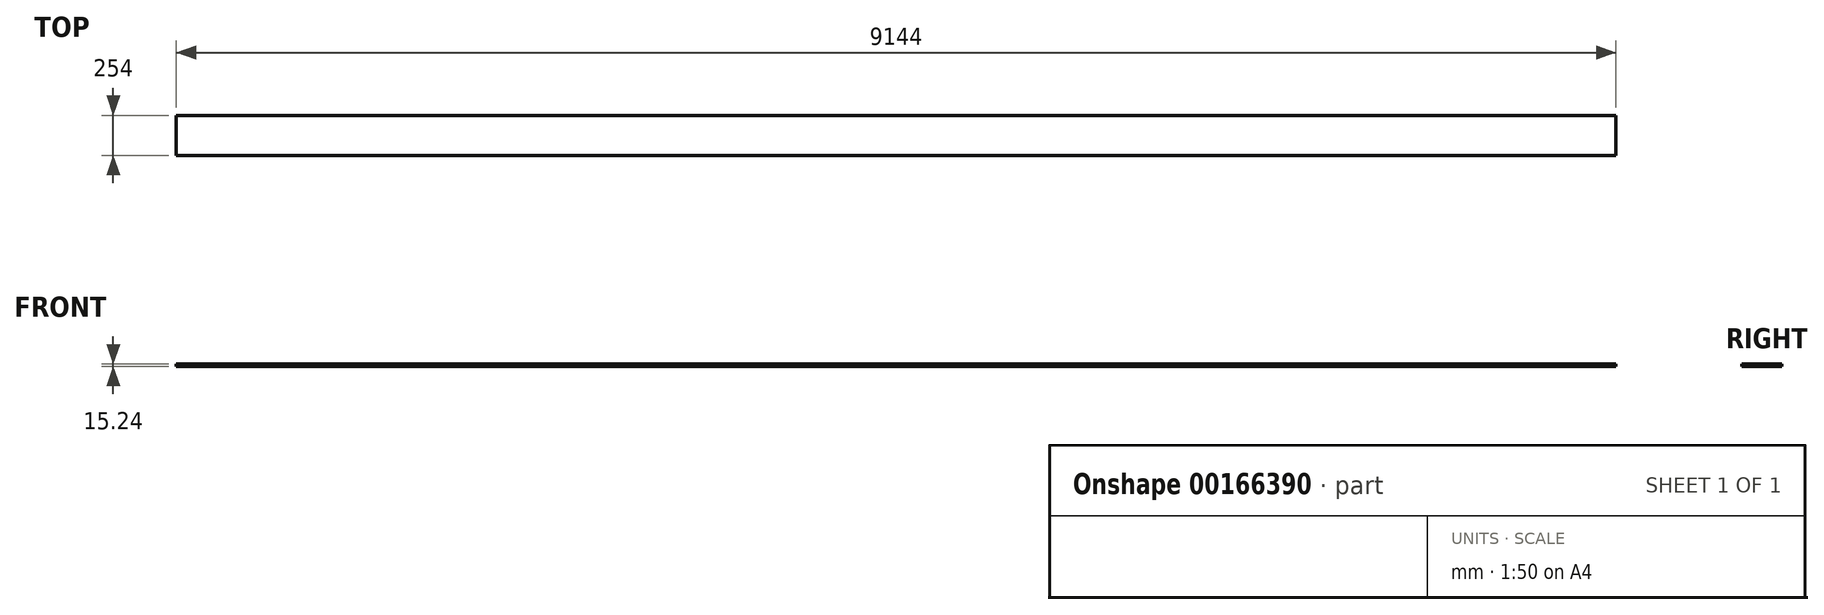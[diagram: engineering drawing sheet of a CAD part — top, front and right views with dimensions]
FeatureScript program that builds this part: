
annotation { "Feature Type Name" : "Feature", "Feature Type Description" : "" }
export const myFeature = defineFeature(function(context is Context, id is Id, definition is map)
    precondition{}
    {
        {
            var Q0;
            Q0=qCreatedBy(makeId("Top.planeOp"),FACE);
            var sketch = newSketch(context, id + "F0", { "sketchPlane" : qUnion([Q0])});
            skLineSegment(sketch, "E0.bottom", {"start": v(4572, -127) * mm, "end": v(-4572, -127) * mm});
            skLineSegment(sketch, "E0.top", {"start": v(4572, 127) * mm, "end": v(-4572, 127) * mm});
            skLineSegment(sketch, "E0.left", {"start": v(4572, -127) * mm, "end": v(4572, 127) * mm});
            skLineSegment(sketch, "E0.right", {"start": v(-4572, -127) * mm, "end": v(-4572, 127) * mm});
            skPoint(sketch, "E0.middle", {"position": v(0, 0) * mm});
            skSolve(sketch);
        }
        {
            var Q0;
            Q0=makeQuery(id+"F0.imprint","IMPRINT",FACE,{"disambiguationData":[TD([[makeQuery(id+"F0.imprint","IMPRINT",EDGE,{"derivedFrom":sQuery(id+"F0.wireOp",EDGE,"E0.bottom")}),-1.0]])]});
            extrude(context, id + "F1", {"entities" : qUnion([Q0]), "depth" : 15.24 * mm});
        }
    });
